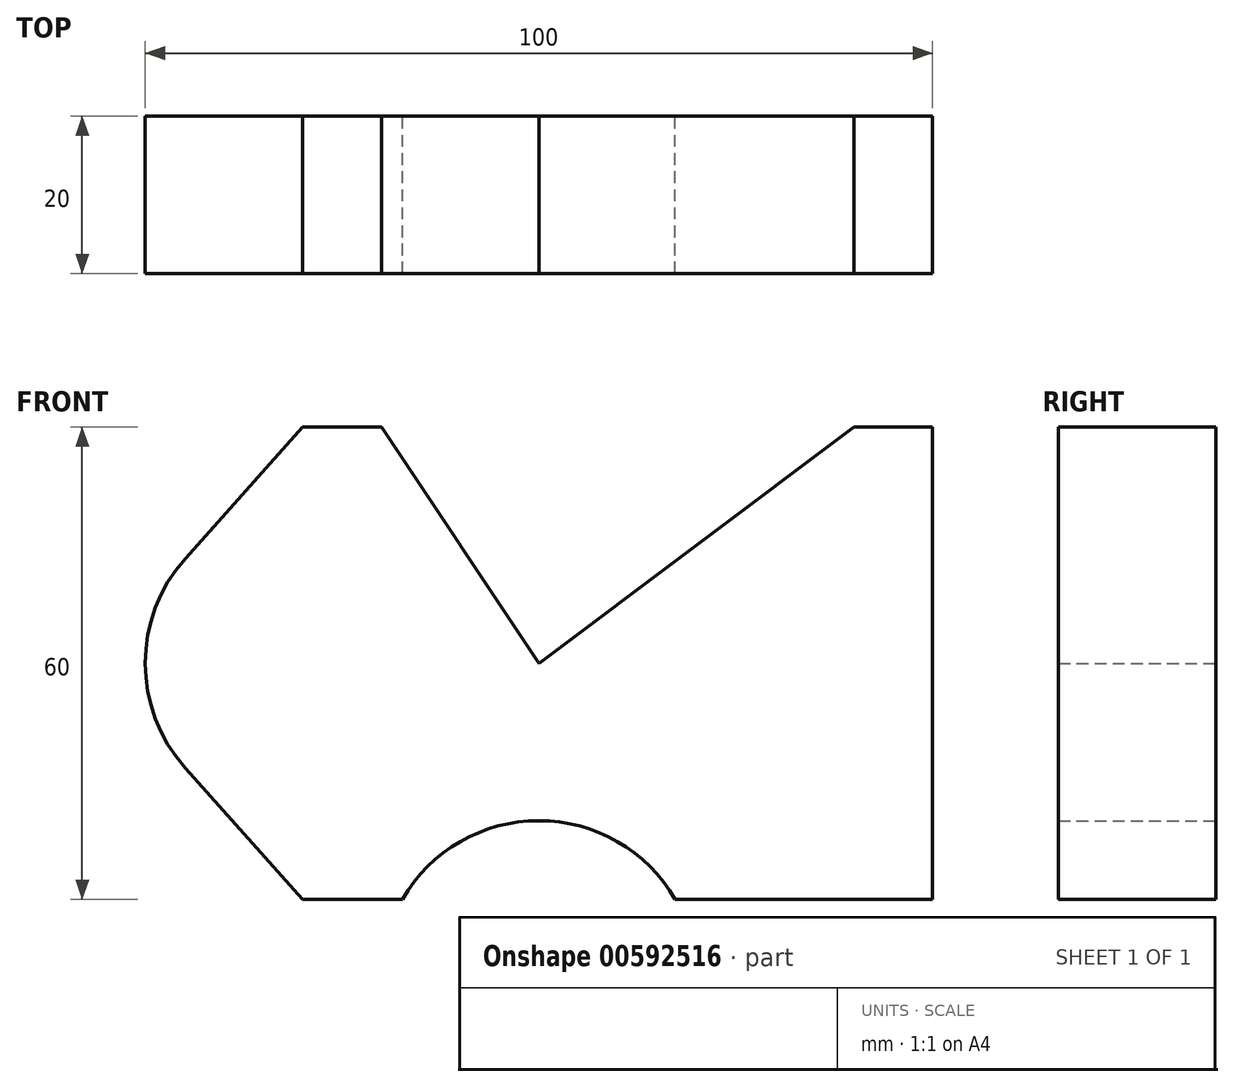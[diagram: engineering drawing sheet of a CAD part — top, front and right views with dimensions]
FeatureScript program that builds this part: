
annotation { "Feature Type Name" : "Feature", "Feature Type Description" : "" }
export const myFeature = defineFeature(function(context is Context, id is Id, definition is map)
    precondition{}
    {
        {
            var Q0;
            Q0=qCreatedBy(makeId("Front.planeOp"),FACE);
            var sketch = newSketch(context, id + "F0", { "sketchPlane" : qUnion([Q0])});
            skLineSegment(sketch, "E0", {"start": v(0, 0) * mm, "end": v(40, 30) * mm});
            skLineSegment(sketch, "E1", {"start": v(40, 30) * mm, "end": v(50, 30) * mm});
            skLineSegment(sketch, "E2", {"start": v(50, 30) * mm, "end": v(50, -30) * mm});
            skLineSegment(sketch, "E3", {"start": v(50, -30) * mm, "end": v(17.32, -30) * mm});
            skArc(sketch, "E4", {"start": v(17.32, -30) * mm, "mid": v(0, -20) * mm, "end": v(-17.32, -30) * mm});
            skLineSegment(sketch, "E5", {"start": v(-17.32, -30) * mm, "end": v(-30, -30) * mm});
            skLineSegment(sketch, "E6", {"start": v(-44.9, 13.33) * mm, "end": v(-30, 30) * mm});
            skLineSegment(sketch, "E7", {"start": v(-30, 30) * mm, "end": v(-20, 30) * mm});
            skLineSegment(sketch, "E8", {"start": v(-20, 30) * mm, "end": v(0, 0) * mm});
            skLineSegment(sketch, "E9", {"start": v(-30, 55.29) * mm, "end": v(-30, -98.23) * mm, "construction": true});
            skLineSegment(sketch, "E10", {"start": v(-30, -30) * mm, "end": v(-44.9, -13.33) * mm});
            skArc(sketch, "E11", {"start": v(-44.9, 13.33) * mm, "mid": v(-50, 0) * mm, "end": v(-44.9, -13.33) * mm});
            skSolve(sketch);
        }
        {
            var Q0;
            Q0=makeQuery(id+"F0.imprint","IMPRINT",FACE,{"disambiguationData":[TD([[makeQuery(id+"F0.imprint","IMPRINT",EDGE,{"derivedFrom":sQuery(id+"F0.wireOp",EDGE,"E0")}),-1.0]])]});
            extrude(context, id + "F1", {"entities" : qUnion([Q0]), "depth" : 20 * mm, "offsetDistance" : 25 * mm});
        }
    });
